# Revit family: Basin_With_Everclean-Wall_Mounted-American_Standard-Murro-0954_Series
name_source: partatom
category: Plumbing Fixtures
revit_build: Autodesk Revit 2014 (Build: 20130308_1515(x64)
units: mm (PartAtom-declared; Revit-internal decimal feet)

## types (10) — shared parameters
ADA Compliant = No
Assembly Code = D2020
Basin Shape = Square
CW Connection = Yes
CWFU = 1.5
Cold Water Connection Diameter = 1/2"
Cold Water Connection Height = 25 1/2"
Cold Water Connection Radius = 1/4"
Cold Water Connection Width = 2"
Default Elevation = 34"
HW Connection = Yes
HWFU = 1.5
Height = 16"
Hot Water Connection Diameter = 1/2"
Hot Water Connection Height = 25 1/2"
Hot Water Connection Radius = 1/4"
Hot Water Connection Width = 2"
Installation Type = Wall Mounted
Length = 20 1/2"
Manufacturer = American Standard
Masterformat Number = 22 41 16
Masterformat Title = Residential Lavatories and Sinks
Material = Vitreous China-American Standard-020-White
Price = Prices may vary. Please consult Manufacturer Representative for most up-to-date price list.
Product Documentation Link = http://www.americanstandard-us.com
Product Page URL = http://www.americanstandard-us.com
URL = http://www.americanstandard-us.com
Vent Connection = No
WFU = 2
Waste Connection = Yes
Waste Connection Diameter = 1 1/4"
Waste Connection Height = 23 1/2"
Waste Connection Radius = 5/8"
Width = 21 1/4"

## per-type parameters (varying)
| type | Description | Model | Void Visibility | Void Visibility 2 | Void Visibility 3 | Void Visibility 4 | Void Visibility 5 |
| 0954.004EC | Wall-Hung Lavatory With Everclean. 4" Centres with overflow. | 0954.004EC | 0" | 2" | 2" | 2" | 4" |
| 0954.123EC | Wall-Hung Lavatory With Everclean. 4" Centres with overflow and extra right-hand hole. | 0954.123EC | 0" | 2" | 0" | 2" | 4" |
| 0954.121EC | Wall-Hung Lavatory With Everclean. 4" Centres with overflow and extra left-hand hole. | 0954.121EC | 0" | 2" | 2" | 0" | 4" |
| 0954.904EC | Wall-Hung Lavatory With Everclean. 4" Centres with less overflow. | 0954.904EC | 0" | 2" | 2" | 2" | 7" |
| 0958.008EC | Wall-Hung Lavatory With Everclean. 8" Centres with overflow. | 0958.008EC | 2" | 0" | 2" | 2" | 4" |
| 0958.908EC | Wall-Hung Lavatory With Everclean. 8" Centres with overflow. | 0958.908EC | 2" | 0" | 2" | 2" | 7" |
| 0955.001EC | Wall-Hung Lavatory With Everclean. Centre only with overflow. | 0955.001EC | 2" | 2" | 2" | 2" | 4" |
| 0955.123EC | Wall-Hung Lavatory With Everclean. Centre hole only with overflow and extra right-hand hole. | 0955123EC | 2" | 2" | 0" | 2" | 4" |
| 0955.121EC | Wall-Hung Lavatory With Everclean. Centre hole only with overflow and extra left-hand hole | 0955.121EC | 2" | 2" | 2" | 0" | 4" |
| 0955.901EC | Wall-Hung Lavatory With Everclean. Centre hole only with less overflow. | 0955.901EC | 2" | 2" | 2" | 2" | 7" |

## geometry (parser evidence)
native form markers: Sweep x1
no freeform markers — native parametric forms only
